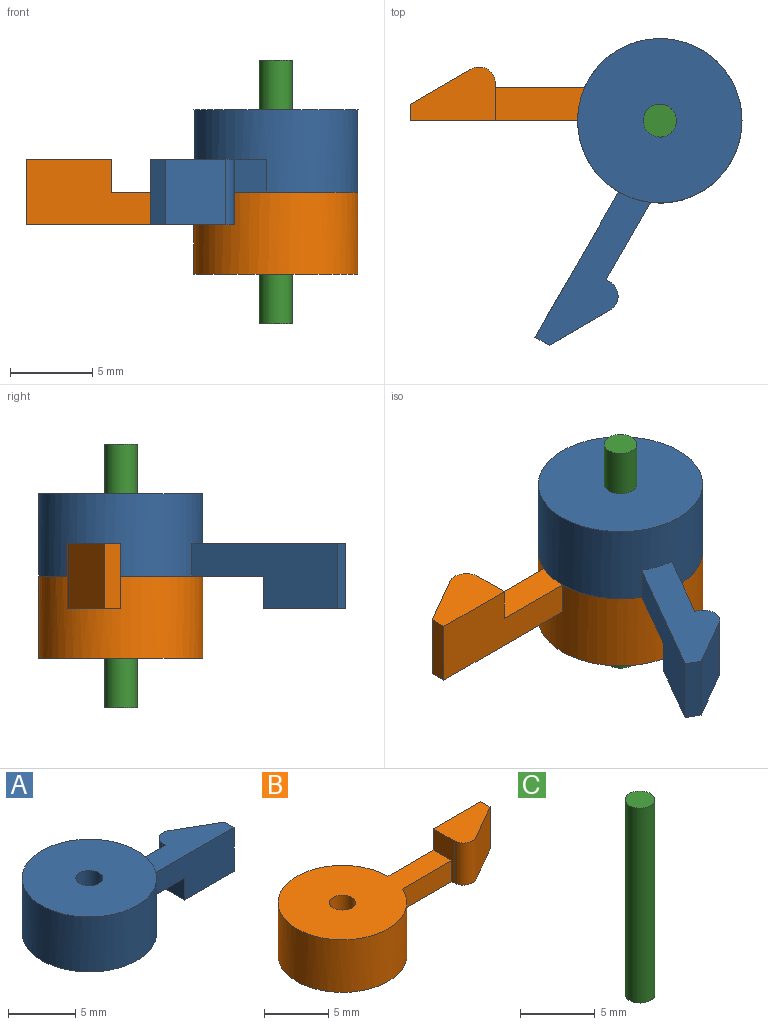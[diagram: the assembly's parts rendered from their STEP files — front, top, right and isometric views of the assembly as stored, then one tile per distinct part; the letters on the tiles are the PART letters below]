
ASSEMBLY  parts=3 mates=2
PART A: 12 faces, bbox 20.2x10x7 mm
  f0: cylinder r=5mm len=10mm, axis (0,0,-1), area 153mm2, adj f1,f2,f3,f4,f5
  f1: plane 10x10mm, normal (0,0,1), area 75.4mm2, adj f0,f11
  f2: plane 15x10mm, normal (0,0,-1), area 85.7mm2, adj f0,f3,f4,f8,f11
  f3: plane 10.2x4mm, normal (0,-1,0), area 30.8mm2, adj f0,f2,f5,f6,f8,f9
  f4: plane 5.42x2mm, normal (0,1,0), area 10.8mm2, adj f0,f2,f5,f8
  f5: plane 10.61x3.27mm, normal (0,0,1), area 22.6mm2, adj f0,f3,f4,f6,f7,f8,f10
  f6: plane 4x1mm, normal (1,0,0), area 4mm2, adj f3,f5,f7,f9
  f7: plane 4x3.7mm, normal (0.5,0.87,0), area 17.1mm2, adj f5,f6,f9,f10
  f8: plane 4x2.27mm, normal (-1,0,0), area 5.1mm2, adj f2,f3,f4,f5,f9,f10
  f9: plane 5.2x3.27mm, normal (0,0,-1), area 12.3mm2, adj f3,f6,f7,f8,f10
  f10: cylinder r=1mm len=4mm, axis (0,0,-1), area 8.4mm2, adj f5,f7,f8,f9
  f11: cylinder r=1mm len=5mm, axis (0,0,-1), area 31.4mm2, adj f1,f2
PART B: 12 faces, bbox 20.2x10x7 mm
  f0: cylinder r=5mm len=10mm, axis (0,0,1), area 153mm2, adj f1,f2,f3,f4,f5
  f1: plane 10x10mm, normal (0,0,-1), area 75.4mm2, adj f0,f11
  f2: plane 15x10mm, normal (0,0,1), area 85.7mm2, adj f0,f3,f4,f6,f11
  f3: plane 10.2x4mm, normal (0,1,0), area 30.8mm2, adj f0,f2,f5,f6,f8,f9
  f4: plane 5.42x2mm, normal (0,-1,0), area 10.8mm2, adj f0,f2,f5,f6
  f5: plane 10.61x3.27mm, normal (0,0,-1), area 22.6mm2, adj f0,f3,f4,f6,f7,f8,f10
  f6: plane 4x2.27mm, normal (-1,0,0), area 5.1mm2, adj f2,f3,f4,f5,f9,f10
  f7: plane 4x3.7mm, normal (0.5,-0.87,0), area 17.1mm2, adj f5,f8,f9,f10
  f8: plane 4x1mm, normal (1,0,0), area 4mm2, adj f3,f5,f7,f9
  f9: plane 5.2x3.27mm, normal (0,0,1), area 12.3mm2, adj f3,f6,f7,f8,f10
  f10: cylinder r=1mm len=4mm, axis (0,0,-1), area 8.4mm2, adj f5,f6,f7,f9
  f11: cylinder r=1mm len=5mm, axis (0,0,1), area 31.4mm2, adj f1,f2
PART C: 3 faces, bbox 2x2x16 mm
  f0: cylinder r=1mm len=16mm, axis (0,0,-1), area 100.5mm2, adj f1,f2
  f1: plane 2x2mm, normal (0,0,1), area 3.1mm2, adj f0
  f2: plane 2x2mm, normal (0,0,-1), area 3.1mm2, adj f0
PLACE A rot(axis=(0,0,-1),120deg) t=(-27.82,-11.59,10.47)mm
PLACE B rot(axis=(0,0,1),180deg) t=(-27.82,-11.59,10.47)mm
PLACE C t=(-27.82,-11.59,10.47)mm fixed
MATE revolute C.f0 <-> B.f0  axis (0,0,-1) through (-27.82,-11.59,10.47)mm
MATE revolute A.f0 <-> C.f0  axis (0,0,-1) through (-27.82,-11.59,10.47)mm
